# Revit family: CWRD
name_source: partatom
category: Lighting Fixtures
revit_build: Autodesk Revit 2014 (Build: 20130308_1515(x64)
units: mm (PartAtom-declared; Revit-internal decimal feet)

## types (1)
- CWRD
    Apparent Load = 1 VA
    Body = Paint - Hubbell - Matte White
    Certification = UL924 Damp Listed, NFPA 101 and NFPA 70
    Default Elevation = 48 "
    Description = The CWR remote head can be applied over path of egress doors and in areas affected by rain, moisture and condensation. Includes mounting base and lamp-heads in durable die-cast construction. Lamp-heads are fully gasketed, fully adjustable and glare-free for operation in outdoor and wet environments. The CWR remote lamps are driven exclusively by the Compass CU2W with remote capacity.
    Features = Constructed of heavy-duty die-cast with glass lens and
chrome-plated metallized reflector
•	 8 LED’s per head using 1.0W at 9.6 VOLTS DC
•	 LED life-cycle of more than 10 years
•	 Operates from 9.6VDC input from the Compass CU2W
Emergency Light
•	 Lamp base mounts to single-gang switch box
•	 Suitable for wall or ceiling mount
    Glass = Glass - Hubbell - White
    Lamp = LED
    Manufacturer = Compass Lighting A unit of Hubbell Lighting
    Model = CWRD
    Product Doucumentation Link = https://hubbellcdn.com
    Product Page URL = https://www.hubbell.com
    Steel = Metal-Hubbell-Galvanized_Steel
    Type Comments = Light Fixture
    URL = https://www.hubbell.com
    Warranty = 2 year full unit warranty
    Wattage Comments = 1W

## geometry (parser evidence)
native form markers: Sweep x1
no freeform markers — native parametric forms only
